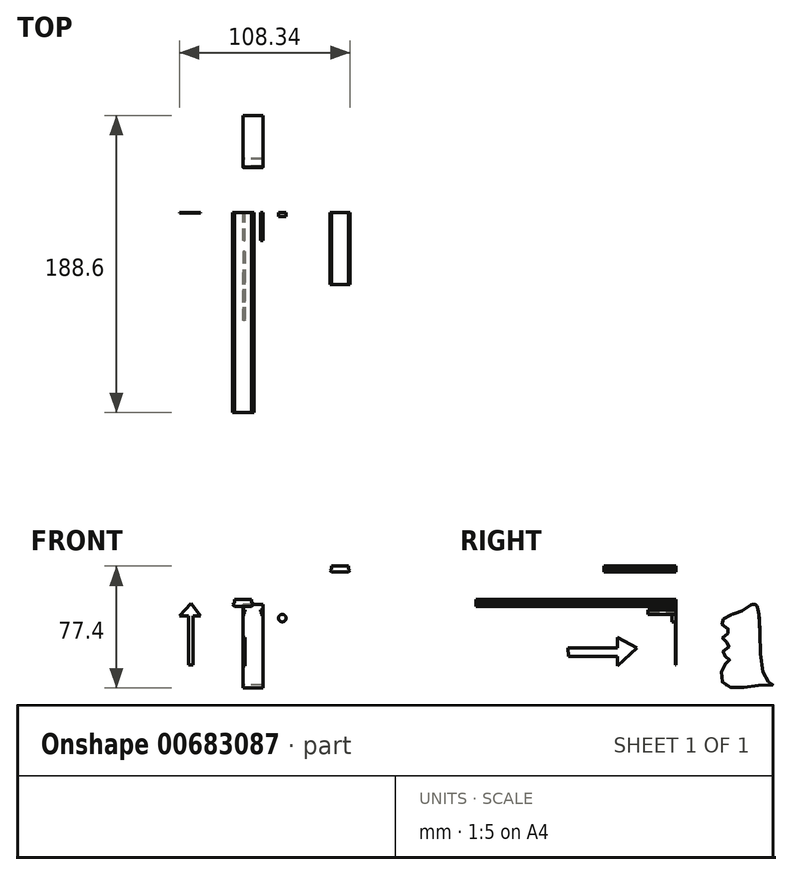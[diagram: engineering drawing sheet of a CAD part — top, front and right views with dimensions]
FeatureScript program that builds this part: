
annotation { "Feature Type Name" : "Feature", "Feature Type Description" : "" }
export const myFeature = defineFeature(function(context is Context, id is Id, definition is map)
    precondition{}
    {
        {
            var Q0;
            Q0=qCreatedBy(makeId("Front.planeOp"),FACE);
            var sketch = newSketch(context, id + "F0", { "sketchPlane" : qUnion([Q0])});
            skCircle(sketch, "E0", {"center": v(0, 0) * mm, "radius": 24 * mm});
            skSolve(sketch);
        }
        {
            var Q0;
            Q0=makeQuery(id+"F0.imprint","IMPRINT",FACE,{"disambiguationData":[TD([[makeQuery(id+"F0.imprint","IMPRINT",EDGE,{"derivedFrom":sQuery(id+"F0.wireOp",EDGE,"E0")}),1.0]])]});
            extrude(context, id + "F1", {"entities" : qUnion([Q0]), "depth" : 127 * mm, "offsetDistance" : 25.4 * mm});
        }
        {
            var Q0;
            Q0=qCreatedBy(makeId("Top.planeOp"),FACE);
            var sketch = newSketch(context, id + "F2", { "sketchPlane" : qUnion([Q0])});
            skLineSegment(sketch, "E1.bottom", {"start": v(-5.64, 0) * mm, "end": v(5.63, 0) * mm});
            skLineSegment(sketch, "E1.top", {"start": v(-5.64, 2.73) * mm, "end": v(5.63, 2.73) * mm});
            skLineSegment(sketch, "E1.left", {"start": v(-5.64, 0) * mm, "end": v(-5.64, 2.73) * mm});
            skLineSegment(sketch, "E1.right", {"start": v(5.63, 0) * mm, "end": v(5.63, 2.73) * mm});
            skLineSegment(sketch, "E2", {"start": v(-5.64, 2.73) * mm, "end": v(-6.65, 3.63) * mm});
            skLineSegment(sketch, "E3", {"start": v(-6.65, 3.63) * mm, "end": v(-5.64, 4.77) * mm});
            skLineSegment(sketch, "E4", {"start": v(-5.64, 4.77) * mm, "end": v(5.63, 4.77) * mm});
            skLineSegment(sketch, "E5", {"start": v(5.63, 4.77) * mm, "end": v(6.68, 3.64) * mm});
            skLineSegment(sketch, "E6", {"start": v(6.68, 3.64) * mm, "end": v(5.63, 2.73) * mm});
            skSolve(sketch);
        }
        {
            var Q0;
            Q0=makeQuery(id+"F2.imprint","IMPRINT",FACE,{"disambiguationData":[TD([[makeQuery(id+"F2.imprint","IMPRINT",EDGE,{"derivedFrom":sQuery(id+"F2.wireOp",EDGE,"E1.bottom")}),1.0]])]});
            var Q1;
            Q1=makeQuery(id+"F2.imprint","IMPRINT",FACE,{"disambiguationData":[TD([[makeQuery(id+"F2.imprint","IMPRINT",EDGE,{"derivedFrom":sQuery(id+"F2.wireOp",EDGE,"E1.top")}),1.0]])]});
            extrude(context, id + "F3", {"entities" : qUnion([Q0, Q1]), "operationType" : NewBodyOperationType.ADD, "endBound" : BoundingType.SYMMETRIC, "depth" : 47 * mm, "offsetDistance" : 25.4 * mm});
        }
        {
            var Q0;
            Q0=qCreatedBy(makeId("Front.planeOp"),FACE);
            var sketch = newSketch(context, id + "F4", { "sketchPlane" : qUnion([Q0])});
            skLineSegment(sketch, "E7.bottom", {"start": v(5.43, -24.06) * mm, "end": v(-5.43, -24.06) * mm});
            skLineSegment(sketch, "E7.top", {"start": v(5.43, -26.37) * mm, "end": v(-5.43, -26.37) * mm});
            skLineSegment(sketch, "E7.left", {"start": v(5.43, -24.06) * mm, "end": v(5.43, -26.37) * mm});
            skLineSegment(sketch, "E7.right", {"start": v(-5.43, -24.06) * mm, "end": v(-5.43, -26.37) * mm});
            skPoint(sketch, "E7.middle", {"position": v(0, -25.21) * mm});
            skLineSegment(sketch, "E8", {"start": v(-5.43, -26.37) * mm, "end": v(-6.48, -27.28) * mm});
            skLineSegment(sketch, "E9", {"start": v(-6.48, -27.28) * mm, "end": v(-5.43, -28.48) * mm});
            skLineSegment(sketch, "E10", {"start": v(-5.43, -28.48) * mm, "end": v(5.43, -28.48) * mm});
            skLineSegment(sketch, "E11", {"start": v(5.43, -28.48) * mm, "end": v(7, -27.28) * mm});
            skLineSegment(sketch, "E12", {"start": v(7, -27.28) * mm, "end": v(5.43, -26.37) * mm});
            skSolve(sketch);
        }
        {
            var Q0;
            Q0 = qSketchRegion(id + "F4", true);
            extrude(context, id + "F5", {"entities" : qUnion([Q0]), "depth" : 127 * mm, "offsetDistance" : 25.4 * mm});
        }
        {
            var Q0;
            Q0=qCreatedBy(makeId("Right.planeOp"),FACE);
            var sketch = newSketch(context, id + "F6", { "sketchPlane" : qUnion([Q0])});
            skPoint(sketch, "E13.12.internal.snap0", {"position": v(30.88, -72.04) * mm});
            skFitSpline(sketch, "E14", {"points": [v(42.54, -30.96) * mm, v(34.12, -34.2) * mm, v(29.08, -39.5) * mm, v(34.12, -44.28) * mm, v(29.63, -49) * mm, v(34.12, -53.28) * mm, v(29.63, -58) * mm, v(34.12, -62.27) * mm, v(30.88, -65.68) * mm, v(30.88, -78.4) * mm, v(56.69, -78.4) * mm, v(61.6, -78.4) * mm, v(55.97, -72.04) * mm, v(50.96, -27.73) * mm, v(42.54, -30.96) * mm]});
            skLineSegment(sketch, "E15", {"start": v(34.95, -33.84) * mm, "end": v(34.95, -33.84) * mm});
            skLineSegment(sketch, "E16", {"start": v(34.95, -33.84) * mm, "end": v(52.8, -33.79) * mm});
            skSolve(sketch);
        }
        {
            var Q0;
            Q0 = qSketchRegion(id + "F6", true);
            extrude(context, id + "F7", {"entities" : qUnion([Q0]), "depth" : 12.7 * mm, "offsetDistance" : 25.4 * mm});
        }
        {
            var Q0;
            Q0=qCreatedBy(makeId("Front.planeOp"),FACE);
            var sketch = newSketch(context, id + "F8", { "sketchPlane" : qUnion([Q0])});
            skLineSegment(sketch, "E17", {"start": v(11.05, -33.67) * mm, "end": v(12.07, -32.66) * mm});
            skLineSegment(sketch, "E18", {"start": v(12.07, -32.66) * mm, "end": v(11.05, -31.65) * mm});
            skLineSegment(sketch, "E19", {"start": v(11.05, -31.65) * mm, "end": v(11.05, -30.67) * mm});
            skLineSegment(sketch, "E20", {"start": v(11.05, -30.67) * mm, "end": v(12.75, -30.67) * mm});
            skLineSegment(sketch, "E21", {"start": v(12.75, -30.67) * mm, "end": v(12.75, -33.67) * mm});
            skLineSegment(sketch, "E22", {"start": v(12.75, -33.67) * mm, "end": v(11.05, -33.67) * mm});
            skLineSegment(sketch, "E23", {"start": v(11.05, -33.67) * mm, "end": v(0, -33.67) * mm});
            skLineSegment(sketch, "E24", {"start": v(0, -33.67) * mm, "end": v(0, -30.67) * mm});
            skLineSegment(sketch, "E25", {"start": v(0, -30.67) * mm, "end": v(1.5, -30.67) * mm});
            skLineSegment(sketch, "E26", {"start": v(1.5, -30.67) * mm, "end": v(1.5, -31.65) * mm});
            skLineSegment(sketch, "E27", {"start": v(1.5, -31.65) * mm, "end": v(0.62, -32.66) * mm});
            skLineSegment(sketch, "E28", {"start": v(0.62, -32.66) * mm, "end": v(1.5, -33.67) * mm});
            skSolve(sketch);
        }
        {
            var Q0;
            Q0 = qSketchRegion(id + "F8", true);
            extrude(context, id + "F9", {"entities" : qUnion([Q0]), "depth" : 17.78 * mm, "offsetDistance" : 25.4 * mm});
        }
        {
            var Q0;
            Q0=qCreatedBy(makeId("Front.planeOp"),FACE);
            var sketch = newSketch(context, id + "F10", { "sketchPlane" : qUnion([Q0])});
            skCircle(sketch, "E29", {"center": v(24.97, -36) * mm, "radius": 2.37 * mm});
            skSolve(sketch);
        }
        {
            var Q0;
            Q0 = qSketchRegion(id + "F10", true);
            extrude(context, id + "F11", {"entities" : qUnion([Q0]), "depth" : 2.54 * mm, "offsetDistance" : 25.4 * mm});
        }
        {
            var Q0;
            Q0=qCreatedBy(makeId("Front.planeOp"),FACE);
            var sketch = newSketch(context, id + "F12", { "sketchPlane" : qUnion([Q0])});
            skLineSegment(sketch, "E30", {"start": v(-34.48, -34.75) * mm, "end": v(-34.48, -65.82) * mm});
            skLineSegment(sketch, "E31", {"start": v(-34.48, -65.82) * mm, "end": v(-31.75, -65.82) * mm});
            skLineSegment(sketch, "E32", {"start": v(-31.75, -65.82) * mm, "end": v(-31.75, -34.75) * mm});
            skLineSegment(sketch, "E33", {"start": v(-31.75, -34.75) * mm, "end": v(-26.84, -34.75) * mm});
            skLineSegment(sketch, "E34", {"start": v(-26.84, -34.75) * mm, "end": v(-32.82, -26.65) * mm});
            skLineSegment(sketch, "E35", {"start": v(-32.82, -26.65) * mm, "end": v(-40.38, -34.75) * mm});
            skLineSegment(sketch, "E36", {"start": v(-40.38, -34.75) * mm, "end": v(-34.48, -34.75) * mm});
            skSolve(sketch);
        }
        {
            var Q0;
            Q0=makeQuery(id+"F12.imprint","IMPRINT",FACE,{"disambiguationData":[TD([[makeQuery(id+"F12.imprint","IMPRINT",EDGE,{"derivedFrom":sQuery(id+"F12.wireOp",EDGE,"E30")}),1.0]])]});
            extrude(context, id + "F13", {"entities" : qUnion([Q0]), "depth" : 0.25 * mm, "offsetDistance" : 25.4 * mm});
        }
        {
            var Q0;
            Q0=qCreatedBy(makeId("Right.planeOp"),FACE);
            var sketch = newSketch(context, id + "F14", { "sketchPlane" : qUnion([Q0])});
            skLineSegment(sketch, "E37", {"start": v(-68.64, -55) * mm, "end": v(-37.03, -55) * mm});
            skLineSegment(sketch, "E38", {"start": v(-37.03, -55) * mm, "end": v(-37.03, -48.18) * mm});
            skLineSegment(sketch, "E39", {"start": v(-37.03, -48.18) * mm, "end": v(-24.81, -55) * mm});
            skLineSegment(sketch, "E40", {"start": v(-24.81, -55) * mm, "end": v(-37.03, -66.5) * mm});
            skLineSegment(sketch, "E41", {"start": v(-37.03, -66.5) * mm, "end": v(-37.03, -60.4) * mm});
            skLineSegment(sketch, "E42", {"start": v(-37.03, -60.4) * mm, "end": v(-68.28, -60.4) * mm});
            skLineSegment(sketch, "E43", {"start": v(-68.28, -60.4) * mm, "end": v(-68.64, -55) * mm});
            skSolve(sketch);
        }
        {
            var Q0;
            Q0=makeQuery(id+"F14.imprint","IMPRINT",FACE,{"disambiguationData":[TD([[makeQuery(id+"F14.imprint","IMPRINT",EDGE,{"derivedFrom":sQuery(id+"F14.wireOp",EDGE,"E37")}),-1.0]])]});
            extrude(context, id + "F15", {"entities" : qUnion([Q0]), "depth" : 1.27 * mm, "offsetDistance" : 25.4 * mm});
        }
        {
            var Q0;
            Q0=qCreatedBy(makeId("Front.planeOp"),FACE);
            var sketch = newSketch(context, id + "F16", { "sketchPlane" : qUnion([Q0])});
            skLineSegment(sketch, "E44", {"start": v(67.06, -2.93) * mm, "end": v(56.4, -2.93) * mm});
            skLineSegment(sketch, "E45", {"start": v(56.4, -2.93) * mm, "end": v(56.4, -5.13) * mm});
            skLineSegment(sketch, "E46", {"start": v(56.4, -5.13) * mm, "end": v(55.43, -5.88) * mm});
            skLineSegment(sketch, "E47", {"start": v(55.43, -5.88) * mm, "end": v(56.4, -6.57) * mm});
            skLineSegment(sketch, "E48", {"start": v(56.4, -6.57) * mm, "end": v(67.06, -6.57) * mm});
            skLineSegment(sketch, "E49", {"start": v(67.06, -6.57) * mm, "end": v(67.96, -5.88) * mm});
            skLineSegment(sketch, "E50", {"start": v(67.96, -5.88) * mm, "end": v(67.06, -5.13) * mm});
            skLineSegment(sketch, "E51", {"start": v(67.06, -5.13) * mm, "end": v(67.06, -2.93) * mm});
            skSolve(sketch);
        }
        {
            var Q0;
            Q0=makeQuery(id+"F16.imprint","IMPRINT",FACE,{"disambiguationData":[TD([[makeQuery(id+"F16.imprint","IMPRINT",EDGE,{"derivedFrom":sQuery(id+"F16.wireOp",EDGE,"E44")}),1.0]])]});
            extrude(context, id + "F17", {"entities" : qUnion([Q0]), "depth" : 45.72 * mm, "offsetDistance" : 25.4 * mm});
        }
        {
            var Q0;
            Q0=makeQuery(id+"F1.opExtrude","SWEPT_BODY",BODY,{"disambiguationData":[OSD([sQuery(id+"F0.wireOp",EDGE,"E0")])]});
            deleteBodies(context, id + "F18", {"entities" : qUnion([Q0])});
        }
    });
